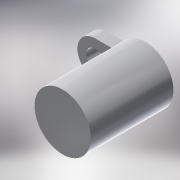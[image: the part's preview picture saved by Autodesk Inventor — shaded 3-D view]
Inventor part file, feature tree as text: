
AUTODESK INVENTOR PART (.ipt)
format: ipt  version: 2018.2 (Build 222227000, 227)  size: 122,880 bytes
history: native  units: mm
features: extrude x2, sketch x1
ambient origin geometry x8: Origin, YZ Plane, XZ Plane, XY Plane, X Axis, Y Axis, Z Axis, Center Point
bodies: Solid1 (feature_tree)
feature tree (3):
  sketch  "Sketch1"  dims[d0=3.0mm d1=9.525mm d2=6.5mm d3=3.0mm d4=2.0mm d5=0.0mm d6=12.0mm d7=0.0mm]
  extrude  "Extrusion1"  Depth=12.0mm
  extrude  "Extrusion2"  Depth=6.5mm
